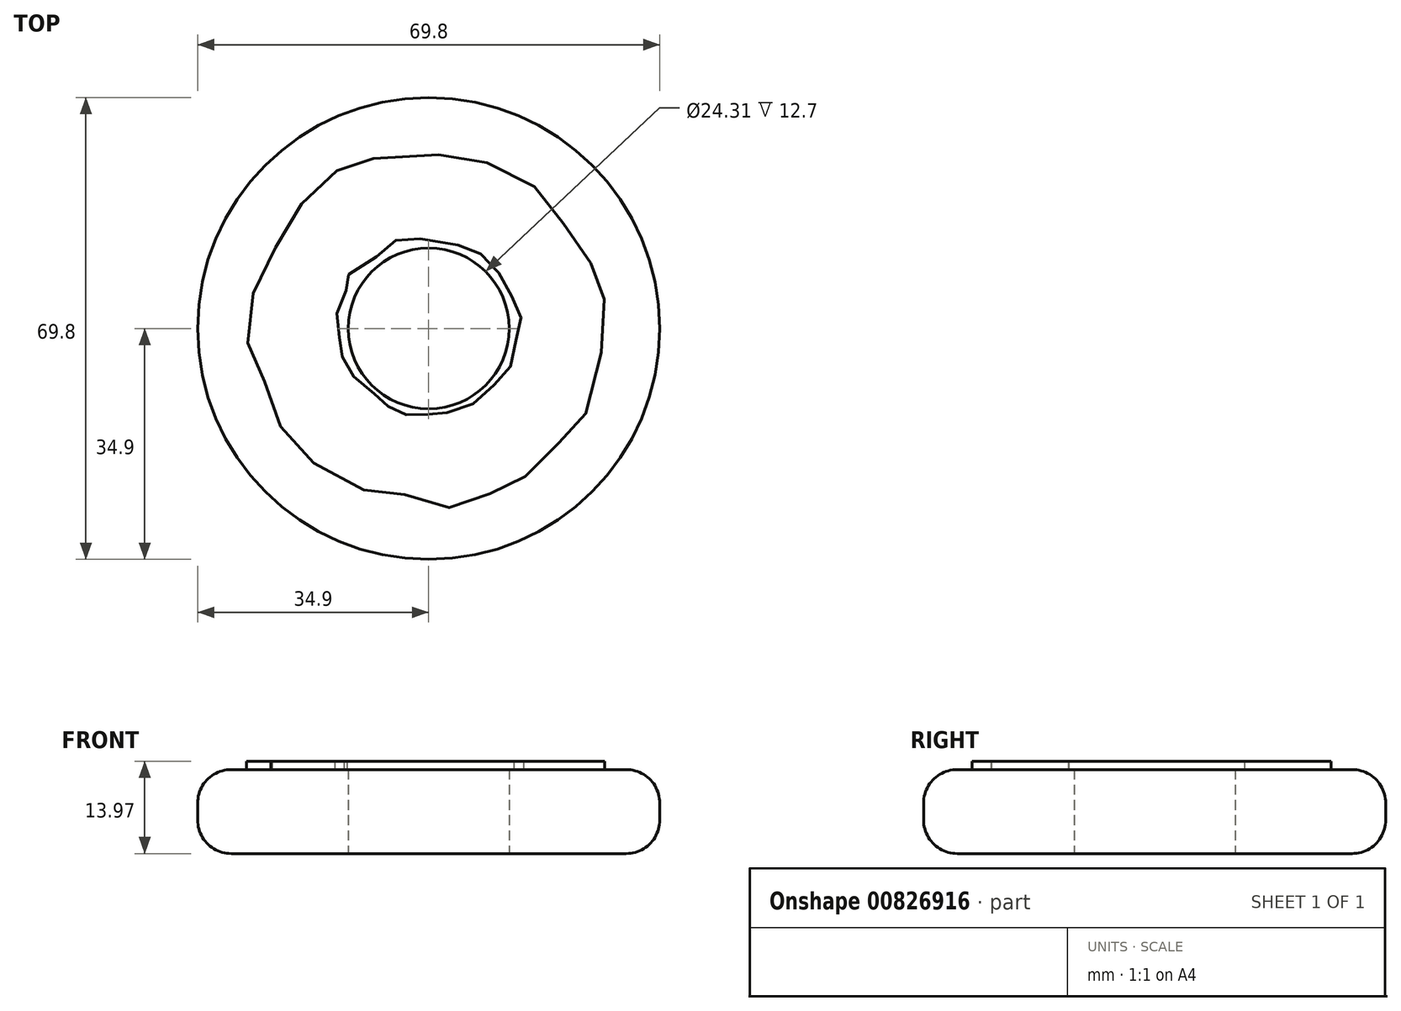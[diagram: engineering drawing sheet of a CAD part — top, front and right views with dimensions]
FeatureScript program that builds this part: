
annotation { "Feature Type Name" : "Feature", "Feature Type Description" : "" }
export const myFeature = defineFeature(function(context is Context, id is Id, definition is map)
    precondition{}
    {
        {
            var Q0;
            Q0=qCreatedBy(makeId("Top.planeOp"),FACE);
            var sketch = newSketch(context, id + "F0", { "sketchPlane" : qUnion([Q0])});
            skCircle(sketch, "E0", {"center": v(0, 0) * mm, "radius": 34.9 * mm});
            skCircle(sketch, "E1", {"center": v(0, 0) * mm, "radius": 12.15 * mm});
            skSolve(sketch);
        }
        {
            var Q0;
            Q0 = qSketchRegion(id + "F0", true);
            extrude(context, id + "F1", {"entities" : qUnion([Q0]), "depth" : 12.7 * mm, "offsetDistance" : 25.4 * mm});
        }
        {
            var Q0;
            Q0=makeQuery(id+"F1.opExtrude","CAP_EDGE",EDGE,{"disambiguationData":[OSD([sQuery(id+"F0.wireOp",EDGE,"E0")])],"isStart":false});
            var Q1;
            Q1=makeQuery(id+"F1.opExtrude","CAP_EDGE",EDGE,{"disambiguationData":[OSD([sQuery(id+"F0.wireOp",EDGE,"E0")])],"isStart":true});
            fillet(context, id + "F2", {"entities" : qUnion([Q0, Q1]), "radius" : 5.08 * mm, "tangentPropagation" : true, "allowEdgeOverflow" : false});
        }
        {
            var Q0;
            Q0=makeQuery(id+"F1.opExtrude","CAP_FACE",FACE,{"disambiguationData":[OSD([sQuery(id+"F0.wireOp",EDGE,"E0"),sQuery(id+"F0.wireOp",EDGE,"E1")])],"isStart":false});
            var sketch = newSketch(context, id + "F3", { "sketchPlane" : qUnion([Q0])});
            skFitSpline(sketch, "E2", {"points": [v(-26.51, 5.3) * mm, v(-25.08, 9.44) * mm, v(-22.44, 13.5) * mm, v(-20.6, 17.76) * mm, v(-16.55, 20.62) * mm, v(-14.3, 23.65) * mm, v(-11.06, 24.48) * mm, v(-9.66, 25.07) * mm, v(-5.18, 26.5) * mm, v(2.95, 26.1) * mm, v(6.8, 25.48) * mm, v(10.45, 24.47) * mm, v(14.92, 22.03) * mm, v(19.18, 19.18) * mm, v(20.41, 15.74) * mm, v(22.23, 13.1) * mm, v(24.88, 9.23) * mm, v(26.09, 7) * mm, v(26.5, 4.58) * mm, v(26.5, 0) * mm, v(25.73, -6) * mm, v(23.84, -12.7) * mm, v(21.84, -14.12) * mm, v(20, -16.75) * mm, v(17.97, -19.19) * mm, v(14.72, -22.23) * mm, v(11.46, -24.07) * mm, v(10.06, -24.86) * mm, v(6.8, -25.3) * mm, v(4.37, -26.5) * mm, v(0, -27.5) * mm, v(-3.36, -25.29) * mm, v(-6.4, -24.69) * mm, v(-8.6, -24.65) * mm, v(-15.19, -22.3) * mm, v(-17.53, -19.95) * mm, v(-18.52, -17.8) * mm, v(-23.69, -13.02) * mm, v(-23.81, -8.67) * mm, v(-26.94, -7.03) * mm, v(-27.38, -2.94) * mm, v(-27.3, 0) * mm, v(-26.51, 5.3) * mm]});
            skFitSpline(sketch, "E3", {"points": [v(-8.23, -9.9) * mm, v(-10.39, -8.31) * mm, v(-12.11, -6.23) * mm, v(-12.9, -4.72) * mm, v(-13.19, -3) * mm, v(-13.33, -1.7) * mm, v(-14.05, 0) * mm, v(-13.76, 2.53) * mm, v(-12.4, 4.9) * mm, v(-12.69, 6.4) * mm, v(-12.76, 6.84) * mm, v(-12.04, 8.2) * mm, v(-8.6, 10.36) * mm, v(-6, 12.65) * mm, v(-4.86, 13.37) * mm, v(-3.78, 13.51) * mm, v(1.1, 13.37) * mm, v(5.34, 12.37) * mm, v(6.77, 11.8) * mm, v(9.93, 9.78) * mm, v(10.65, 8.35) * mm, v(12.01, 6.55) * mm, v(13.02, 3.03) * mm, v(13.74, 2.1) * mm, v(14.17, -0.77) * mm, v(13.02, -2) * mm, v(12.8, -4.36) * mm, v(11.08, -7.67) * mm, v(9.86, -8.53) * mm, v(8.2, -10.47) * mm, v(4.47, -12.26) * mm, v(2.68, -12.76) * mm, v(1.1, -12.98) * mm, v(0, -12.98) * mm, v(-1.7, -13.05) * mm, v(-3.5, -13.05) * mm, v(-4.57, -12.9) * mm, v(-6.22, -11.61) * mm, v(-6.87, -10.68) * mm, v(-8.23, -9.9) * mm]});
            skSolve(sketch);
        }
        {
            var Q0;
            Q0 = qSketchRegion(id + "F3", true);
            extrude(context, id + "F4", {"entities" : qUnion([Q0]), "operationType" : NewBodyOperationType.ADD, "depth" : 1.27 * mm, "offsetDistance" : 25.4 * mm});
        }
    });
